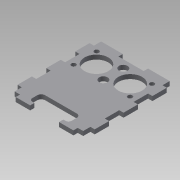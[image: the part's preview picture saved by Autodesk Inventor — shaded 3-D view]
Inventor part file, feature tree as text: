
AUTODESK INVENTOR PART (.ipt)
format: ipt  version: 2015 SP1 (Build 190203100, 203)  size: 163,840 bytes
history: native  units: mm
features: extrude x1, sketch x1
ambient origin geometry x8: Origin, YZ Plane, XZ Plane, XY Plane, X Axis, Y Axis, Z Axis, Center Point
bodies: Solid1 (feature_tree)
feature tree (2):
  extrude  "Extrusion1"  TaperAngle=180.0deg  [1 undecoded]
  sketch  "Sketch1"  dims[d2=20.0mm d4=15.0mm d5=20.0mm d7=15.0mm d10=180.0deg d11=2.0mm d12=3.0mm d14=20.0mm d16=20.0mm d17=20.0mm d19=20.0mm d46=7.675mm d47=7.675mm d48=3.0mm d49=0.0mm]
note: 1 required parameter value undecoded (feature->parameter linkage not recoverable at this tier; creation-order binding heuristic only, values carry confidence <= 0.55)
